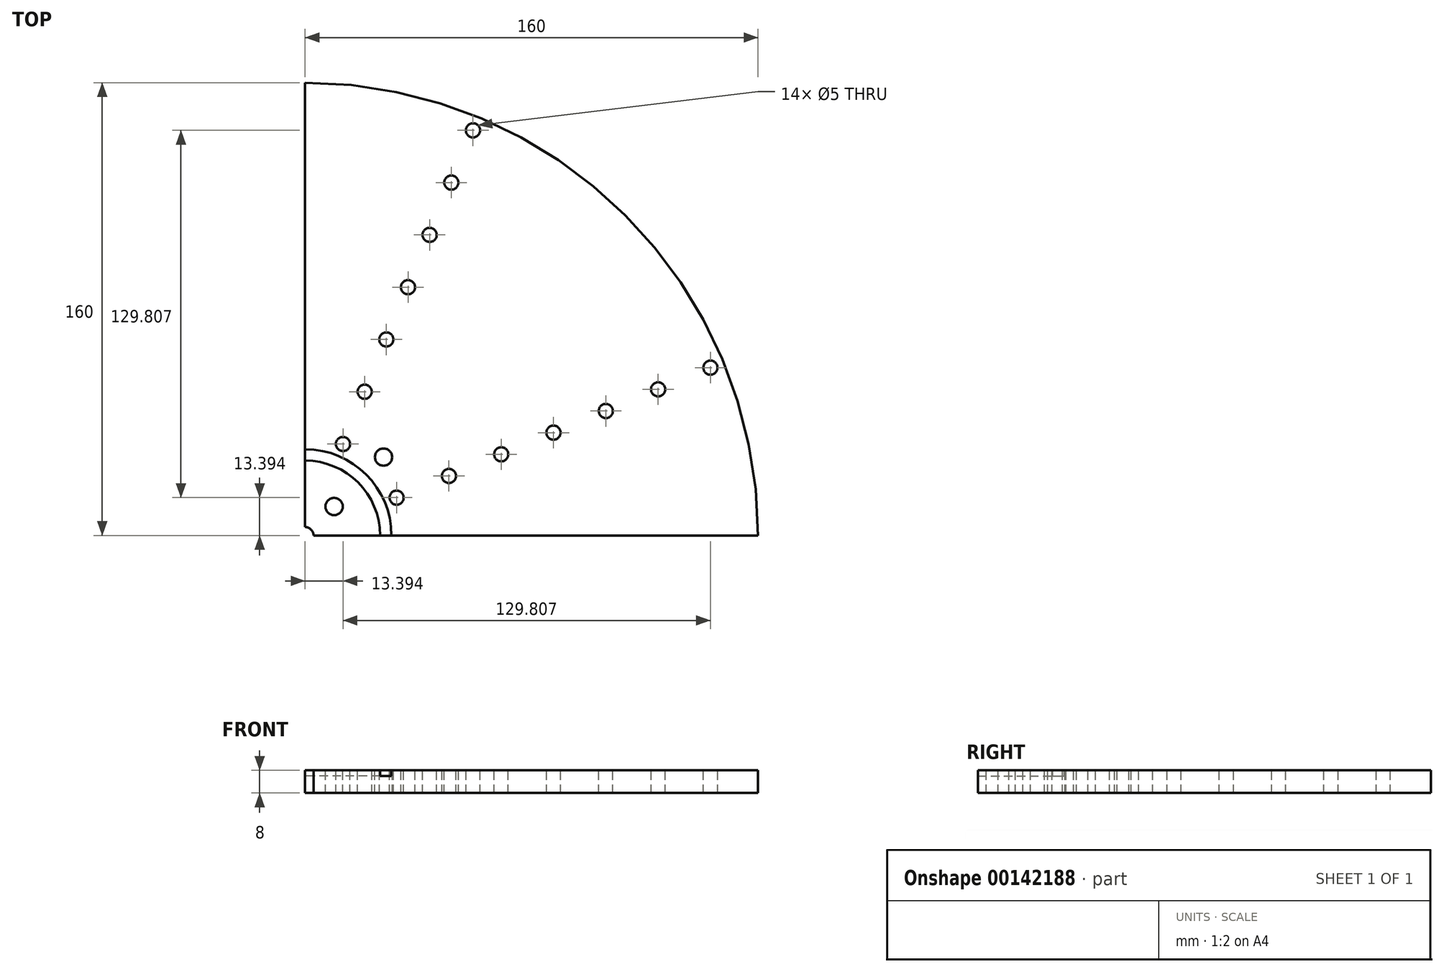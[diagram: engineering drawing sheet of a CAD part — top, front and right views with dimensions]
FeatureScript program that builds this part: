
annotation { "Feature Type Name" : "Feature", "Feature Type Description" : "" }
export const myFeature = defineFeature(function(context is Context, id is Id, definition is map)
    precondition{}
    {
        {
            var Q0;
            Q0=qCreatedBy(makeId("Top.planeOp"),FACE);
            var sketch = newSketch(context, id + "F0", { "sketchPlane" : qUnion([Q0])});
            skArc(sketch, "E0", {"start": v(160, 0) * mm, "mid": v(113.14, 113.14) * mm, "end": v(0, 160) * mm});
            skArc(sketch, "E1", {"start": v(26.5, 0) * mm, "mid": v(18.74, 18.74) * mm, "end": v(0, 26.5) * mm});
            skArc(sketch, "E2", {"start": v(30.5, 0) * mm, "mid": v(21.57, 21.57) * mm, "end": v(0, 30.5) * mm});
            skLineSegment(sketch, "E3", {"start": v(0, 3) * mm, "end": v(0, 160) * mm});
            skLineSegment(sketch, "E4", {"start": v(2.12, 2.12) * mm, "end": v(113.14, 113.14) * mm, "construction": true});
            skLineSegment(sketch, "E5", {"start": v(3, 0) * mm, "end": v(160, 0) * mm});
            skLineSegment(sketch, "E6", {"start": v(1.15, 2.77) * mm, "end": v(61.23, 147.82) * mm, "construction": true});
            skLineSegment(sketch, "E7", {"start": v(2.77, 1.15) * mm, "end": v(147.82, 61.23) * mm, "construction": true});
            skCircle(sketch, "E8", {"center": v(10.25, 10.25) * mm, "radius": 3.05 * mm});
            skCircle(sketch, "E9", {"center": v(27.72, 27.72) * mm, "radius": 3.05 * mm});
            skCircle(sketch, "E10", {"center": v(13.4, 32.34) * mm, "radius": 2.5 * mm});
            skCircle(sketch, "E11", {"center": v(21.05, 50.81) * mm, "radius": 2.5 * mm});
            skCircle(sketch, "E12", {"center": v(28.7, 69.3) * mm, "radius": 2.5 * mm});
            skCircle(sketch, "E13", {"center": v(36.35, 87.77) * mm, "radius": 2.5 * mm});
            skCircle(sketch, "E14", {"center": v(59.32, 143.2) * mm, "radius": 2.5 * mm});
            skCircle(sketch, "E15", {"center": v(44, 106.25) * mm, "radius": 2.5 * mm});
            skCircle(sketch, "E16", {"center": v(51.66, 124.72) * mm, "radius": 2.5 * mm});
            skCircle(sketch, "E17", {"center": v(32.34, 13.4) * mm, "radius": 2.5 * mm});
            skCircle(sketch, "E18", {"center": v(50.81, 21.05) * mm, "radius": 2.5 * mm});
            skCircle(sketch, "E19", {"center": v(69.3, 28.7) * mm, "radius": 2.5 * mm});
            skCircle(sketch, "E20", {"center": v(87.77, 36.35) * mm, "radius": 2.5 * mm});
            skCircle(sketch, "E21", {"center": v(106.25, 44) * mm, "radius": 2.5 * mm});
            skCircle(sketch, "E22", {"center": v(124.72, 51.66) * mm, "radius": 2.5 * mm});
            skCircle(sketch, "E23", {"center": v(143.2, 59.32) * mm, "radius": 2.5 * mm});
            skArc(sketch, "E24", {"start": v(3, 0) * mm, "mid": v(2.12, 2.12) * mm, "end": v(0, 3) * mm});
            skSolve(sketch);
        }
        {
            var Q0;
            {var subQ0=sQuery(id+"F0.wireOp",EDGE,"E0");Q0=makeQuery(id+"F0.imprint","IMPRINT",FACE,{"disambiguationData":[TD([[makeQuery(id+"F0.imprint","IMPRINT",EDGE,{"derivedFrom":subQ0}),1.0]])]});}
            var Q1;
            {var subQ0=sQuery(id+"F0.wireOp",EDGE,"E1");Q1=makeQuery(id+"F0.imprint","IMPRINT",FACE,{"disambiguationData":[TD([[makeQuery(id+"F0.imprint","IMPRINT",EDGE,{"derivedFrom":subQ0}),1.0]])]});}
            var Q2;
            {var subQ0=sQuery(id+"F0.wireOp",EDGE,"E1");Q2=makeQuery(id+"F0.imprint","IMPRINT",FACE,{"disambiguationData":[TD([[makeQuery(id+"F0.imprint","IMPRINT",EDGE,{"derivedFrom":subQ0}),-1.0]])]});}
            extrude(context, id + "F1", {"entities" : qUnion([Q0, Q1, Q2]), "oppositeDirection" : true, "depth" : 8 * mm, "offsetDistance" : 25 * mm});
        }
        {
            var Q0;
            {var subQ0=sQuery(id+"F0.wireOp",EDGE,"E1");Q0=makeQuery(id+"F0.imprint","IMPRINT",FACE,{"disambiguationData":[TD([[makeQuery(id+"F0.imprint","IMPRINT",EDGE,{"derivedFrom":subQ0}),-1.0]])]});}
            extrude(context, id + "F2", {"entities" : qUnion([Q0]), "operationType" : NewBodyOperationType.REMOVE, "oppositeDirection" : true, "depth" : 2 * mm, "offsetDistance" : 25 * mm});
        }
    });
